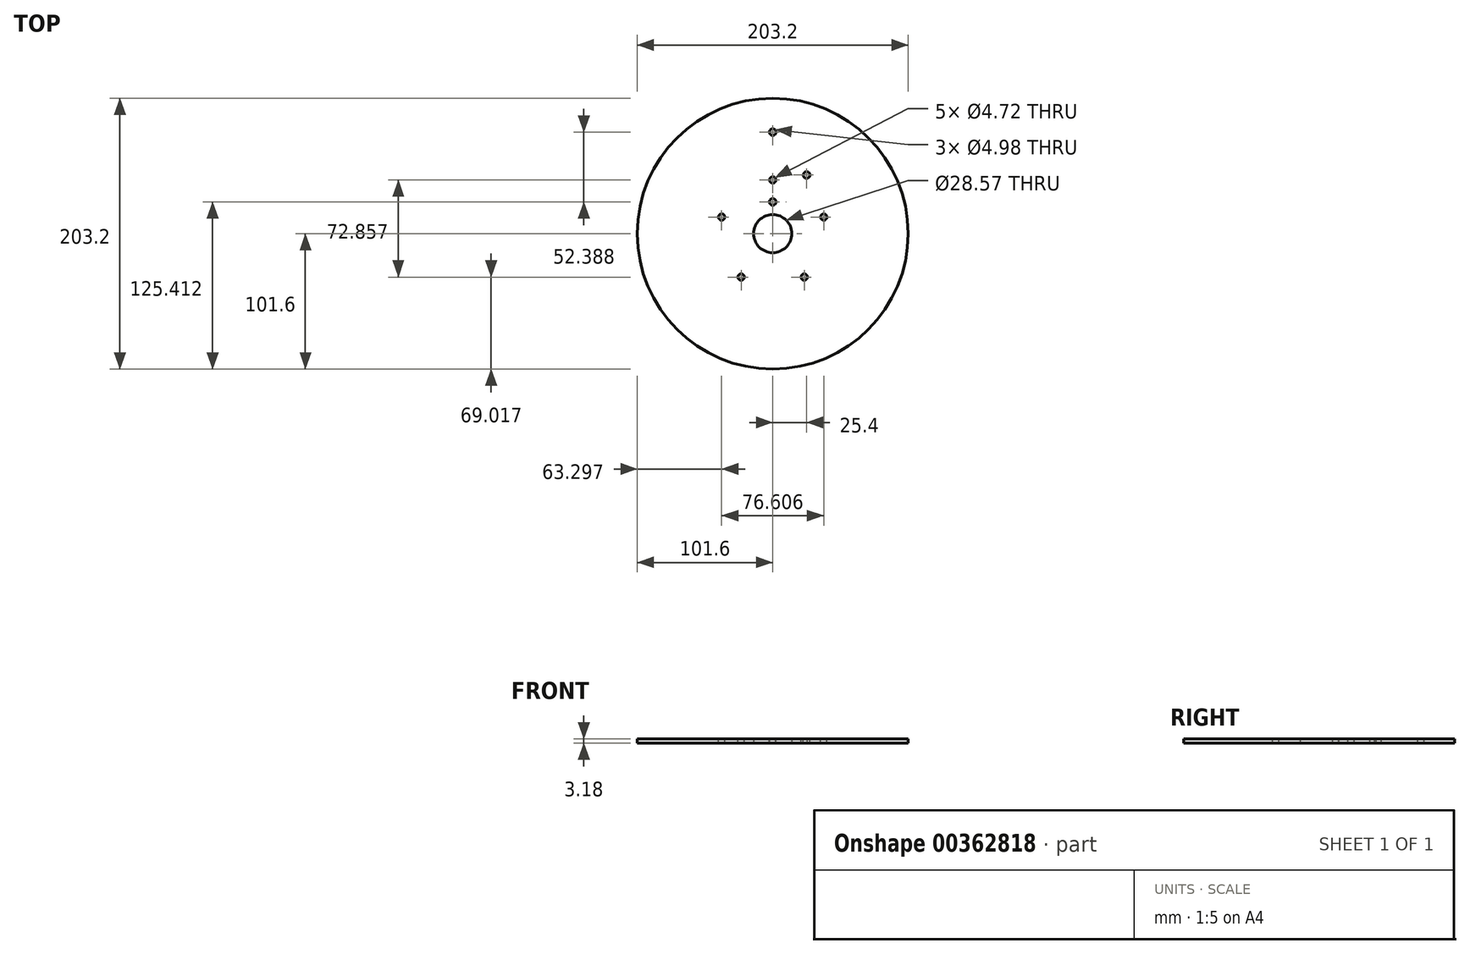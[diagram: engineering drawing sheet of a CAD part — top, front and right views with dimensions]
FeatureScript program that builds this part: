
annotation { "Feature Type Name" : "Feature", "Feature Type Description" : "" }
export const myFeature = defineFeature(function(context is Context, id is Id, definition is map)
    precondition{}
    {
        {
            var Q0;
            Q0=qCreatedBy(makeId("Top.planeOp"),FACE);
            var sketch = newSketch(context, id + "F0", { "sketchPlane" : qUnion([Q0])});
            skCircle(sketch, "E0", {"center": v(0, 0) * mm, "radius": 101.6 * mm});
            skCircle(sketch, "E1", {"center": v(0, 0) * mm, "radius": 14.29 * mm});
            skSolve(sketch);
        }
        {
            var Q0;
            Q0=makeQuery(id+"F0.imprint","IMPRINT",FACE,{"disambiguationData":[TD([[makeQuery(id+"F0.imprint","IMPRINT",EDGE,{"derivedFrom":sQuery(id+"F0.wireOp",EDGE,"E0")}),1.0]])]});
            extrude(context, id + "F1", {"entities" : qUnion([Q0]), "depth" : 3.17 * mm});
        }
        {
            var Q0;
            Q0=makeQuery(id+"F1.opExtrude","CAP_FACE",FACE,{"disambiguationData":[OSD([sQuery(id+"F0.wireOp",EDGE,"E0"),sQuery(id+"F0.wireOp",EDGE,"E1")])],"isStart":false});
            var sketch = newSketch(context, id + "F2", { "sketchPlane" : qUnion([Q0])});
            skCircle(sketch, "E2", {"center": v(0, 23.81) * mm, "radius": 2.49 * mm});
            skCircle(sketch, "E3", {"center": v(0, 76.2) * mm, "radius": 2.49 * mm});
            skCircle(sketch, "E4", {"center": v(25.4, 44) * mm, "radius": 2.49 * mm});
            skLineSegment(sketch, "E5", {"start": v(0, 0) * mm, "end": v(25.4, 44) * mm, "construction": true});
            skSolve(sketch);
        }
        {
            var Q0;
            Q0=qSketchRegion(id+"F2",true);
            extrude(context, id + "F3", {"entities" : qUnion([Q0]), "operationType" : NewBodyOperationType.REMOVE, "endBound" : BoundingType.THROUGH_ALL, "oppositeDirection" : true, "depth" : 25.4 * mm});
        }
        {
            var Q0;
            Q0=makeQuery(id+"F1.opExtrude","CAP_FACE",FACE,{"disambiguationData":[OSD([sQuery(id+"F0.wireOp",EDGE,"E0"),sQuery(id+"F0.wireOp",EDGE,"E1")])],"isStart":false});
            var sketch = newSketch(context, id + "F4", { "sketchPlane" : qUnion([Q0])});
            skCircle(sketch, "E6.cCircle", {"center": v(0, 0) * mm, "radius": 32.58 * mm, "construction": true});
            skLineSegment(sketch, "E6.0", {"start": v(23.67, -32.58) * mm, "end": v(-23.67, -32.58) * mm, "construction": true});
            skLineSegment(sketch, "E6.1", {"start": v(-23.67, -32.58) * mm, "end": v(-38.3, 12.45) * mm, "construction": true});
            skLineSegment(sketch, "E6.2", {"start": v(-38.3, 12.45) * mm, "end": v(0, 40.27) * mm, "construction": true});
            skLineSegment(sketch, "E6.3", {"start": v(0, 40.27) * mm, "end": v(38.3, 12.45) * mm, "construction": true});
            skLineSegment(sketch, "E6.4", {"start": v(38.3, 12.45) * mm, "end": v(23.67, -32.58) * mm, "construction": true});
            skPoint(sketch, "E6.0.midPoint", {"position": v(0, -32.58) * mm});
            skCircle(sketch, "E7", {"center": v(0, 40.27) * mm, "radius": 2.36 * mm});
            skCircle(sketch, "E8", {"center": v(38.3, 12.45) * mm, "radius": 2.36 * mm});
            skCircle(sketch, "E9", {"center": v(23.67, -32.58) * mm, "radius": 2.36 * mm});
            skCircle(sketch, "E10", {"center": v(-23.67, -32.58) * mm, "radius": 2.36 * mm});
            skCircle(sketch, "E11", {"center": v(-38.3, 12.45) * mm, "radius": 2.36 * mm});
            skCircle(sketch, "E12", {"center": v(0, 0) * mm, "radius": 40.27 * mm, "construction": true});
            skSolve(sketch);
        }
        {
            var Q0;
            Q0 = qSketchRegion(id + "F4", true);
            extrude(context, id + "F5", {"entities" : qUnion([Q0]), "operationType" : NewBodyOperationType.REMOVE, "endBound" : BoundingType.THROUGH_ALL, "oppositeDirection" : true, "depth" : 25.4 * mm});
        }
    });
